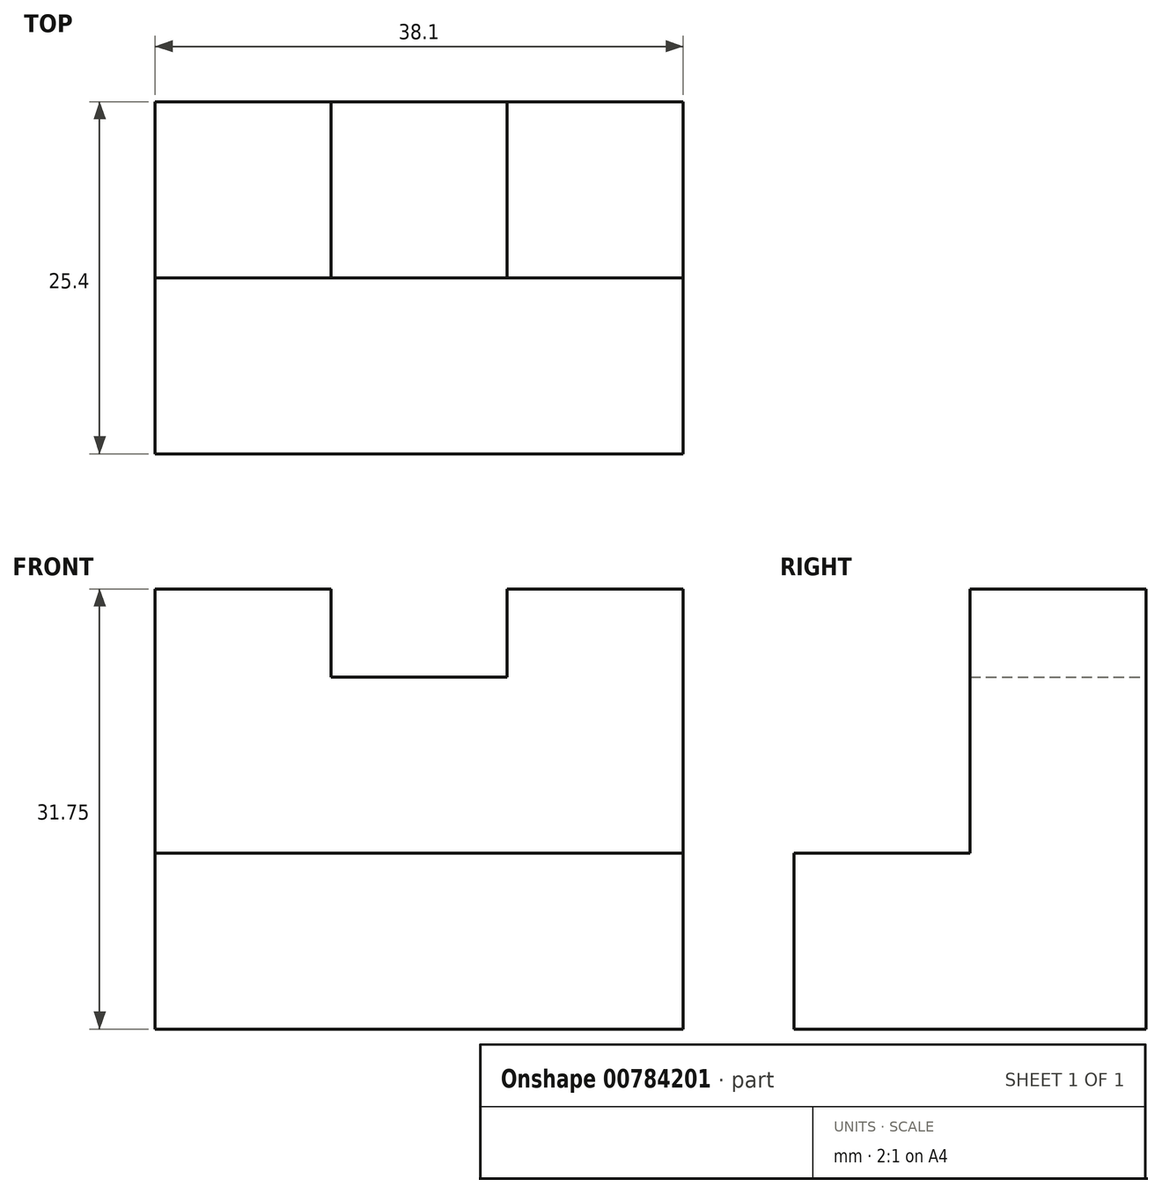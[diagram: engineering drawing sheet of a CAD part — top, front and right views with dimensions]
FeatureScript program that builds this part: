
annotation { "Feature Type Name" : "Feature", "Feature Type Description" : "" }
export const myFeature = defineFeature(function(context is Context, id is Id, definition is map)
    precondition{}
    {
        {
            var Q0;
            Q0=qCreatedBy(makeId("Front.planeOp"),FACE);
            var sketch = newSketch(context, id + "F0", { "sketchPlane" : qUnion([Q0])});
            skLineSegment(sketch, "E0", {"start": v(0, 0) * mm, "end": v(0, 31.75) * mm});
            skLineSegment(sketch, "E1", {"start": v(0, 31.75) * mm, "end": v(12.7, 31.75) * mm});
            skLineSegment(sketch, "E2", {"start": v(12.7, 31.75) * mm, "end": v(12.7, 25.4) * mm});
            skLineSegment(sketch, "E3", {"start": v(12.7, 25.4) * mm, "end": v(25.4, 25.4) * mm});
            skLineSegment(sketch, "E4", {"start": v(25.4, 25.4) * mm, "end": v(25.4, 31.75) * mm});
            skLineSegment(sketch, "E5", {"start": v(25.4, 31.75) * mm, "end": v(38.1, 31.75) * mm});
            skLineSegment(sketch, "E6", {"start": v(38.1, 31.75) * mm, "end": v(38.1, 0) * mm});
            skLineSegment(sketch, "E7", {"start": v(38.1, 0) * mm, "end": v(0, 0) * mm});
            skSolve(sketch);
        }
        {
            var Q0;
            Q0 = qSketchRegion(id + "F0", true);
            extrude(context, id + "F1", {"entities" : qUnion([Q0]), "depth" : 25.4 * mm, "offsetDistance" : 25.4 * mm});
        }
        {
            var Q0;
            Q0=makeQuery(id+"F1.opExtrude","SWEPT_FACE",FACE,{"disambiguationData":[OSD([sQuery(id+"F0.wireOp",EDGE,"E5")])]});
            var sketch = newSketch(context, id + "F2", { "sketchPlane" : qUnion([Q0])});
            skLineSegment(sketch, "E8", {"start": v(38.1, -25.4) * mm, "end": v(38.1, -12.7) * mm});
            skLineSegment(sketch, "E9", {"start": v(38.1, -12.7) * mm, "end": v(25.4, -12.7) * mm});
            skLineSegment(sketch, "E10", {"start": v(25.4, -12.7) * mm, "end": v(25.4, -25.4) * mm});
            skLineSegment(sketch, "E11", {"start": v(25.4, -25.4) * mm, "end": v(38.1, -25.4) * mm});
            skSolve(sketch);
        }
        {
            var Q0;
            Q0 = qSketchRegion(id + "F2", true);
            extrude(context, id + "F3", {"entities" : qUnion([Q0]), "operationType" : NewBodyOperationType.REMOVE, "depth" : 25.4 * mm, "offsetDistance" : 25.4 * mm});
        }
        {
            var Q0;
            Q0=makeQuery(id+"F1.opExtrude","SWEPT_FACE",FACE,{"disambiguationData":[OSD([sQuery(id+"F0.wireOp",EDGE,"E6")])]});
            var sketch = newSketch(context, id + "F4", { "sketchPlane" : qUnion([Q0])});
            skLineSegment(sketch, "E12", {"start": v(-25.4, 31.75) * mm, "end": v(-12.7, 31.75) * mm});
            skLineSegment(sketch, "E13", {"start": v(-12.7, 31.75) * mm, "end": v(-12.7, 12.7) * mm});
            skLineSegment(sketch, "E14", {"start": v(-12.7, 12.7) * mm, "end": v(-25.4, 12.7) * mm});
            skLineSegment(sketch, "E15", {"start": v(-12.7, 31.75) * mm, "end": v(-25.4, 31.75) * mm});
            skLineSegment(sketch, "E16", {"start": v(-25.4, 31.75) * mm, "end": v(-25.4, 12.7) * mm});
            skSolve(sketch);
        }
        {
            var Q0;
            Q0=makeQuery(id+"F4.imprint","IMPRINT",FACE,{"disambiguationData":[TD([[makeQuery(id+"F4.imprint","IMPRINT",EDGE,{"derivedFrom":sQuery(id+"F4.wireOp",EDGE,"E13")}),-1.0]])]});
            extrude(context, id + "F5", {"entities" : qUnion([Q0]), "operationType" : NewBodyOperationType.REMOVE, "oppositeDirection" : true, "depth" : 38.1 * mm, "offsetDistance" : 25.4 * mm});
        }
    });
